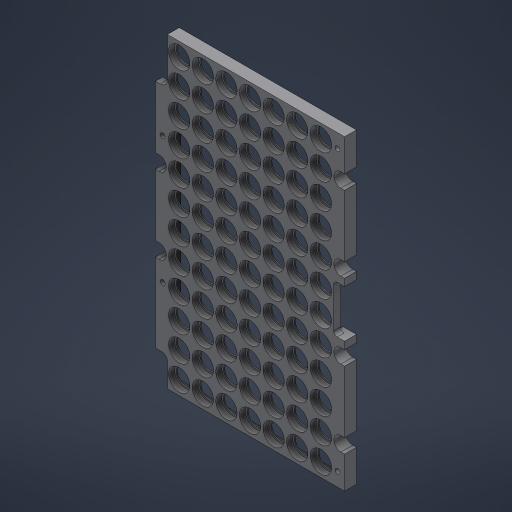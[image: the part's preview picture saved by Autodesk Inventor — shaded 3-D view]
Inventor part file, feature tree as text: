
AUTODESK INVENTOR PART (.ipt)
format: ipt  version: 2024.3 (Build 283343010, 343A)  size: 755,200 bytes
history: native  units: mm
features: extrude x4, sketch x3, hole x3, pattern_linear x1, fillet x1
ambient origin geometry x8: Origin, YZ Plane, XZ Plane, XY Plane, X Axis, Y Axis, Z Axis, Center Point
bodies: Volumenkörper1 (feature_tree)
feature tree (12):
  sketch  "Skizze1"  dims[d0=160.0mm d1=260.0mm]
  extrude  "Extrusion1"  Depth=260.0mm
  hole  "Bohrung1"  [1 undecoded]
  pattern_linear  "Rechteckige Anordnung1"  Count1=6 Spacing1=43.0mm
  sketch  "Skizze2"  dims[d2=10.0mm d3=0.0mm d4=18.0mm d5=60.0mm d7=43.0mm d8=70.0mm d10=20.0mm]
  extrude  "Extrusion4"  Depth=3.0mm
  hole  "Bohrung4"  [1 undecoded]
  sketch  "Skizze4"  dims[d16=21.5mm d19=70.0mm d21=20.0mm d22=60.0mm d24=43.0mm d69=15.0mm d70=15.0mm d71=6.0mm d72=18.0mm d73=5.0mm d74=90.0deg d75=8.0mm d76=20.594885mm d77=70.0mm d79=20.0mm d80=0.0mm d83=10.0mm d84=5.0mm d85=60.0mm d101=25.0mm d113=157.7mm d119=8.0mm d121=6.0mm d124=33.25mm d125=64.5mm d126=6.0mm d127=10.75mm d129=7.0mm d130=7.0mm d132=3.0mm d134=10.75mm d135=9.5mm d136=3.0mm d140=10.0mm d141=0.0mm d142=6.0mm d143=4.0mm d144=5.0mm d145=4.0mm d146=6.0mm d147=4.0mm d148=2.0mm d149=90.0deg d150=8.0mm d151=20.594885mm d152=4.0mm d153=6.0mm d154=6.0mm d155=5.0mm d156=90.0deg d157=8.0mm d158=20.594885mm d160=8.0mm d162=3.0mm d165=20.0mm d166=5.75mm d169=7.0mm d170=7.0mm d171=3.64mm d172=10.75mm d180=2.0mm d181=2.0mm d182=5.0mm d184=8.75mm d185=8.75mm d186=4.0mm d187=0.0mm d190=40.0mm d191=20.0mm d192=0.0mm d193=0.0mm d195=60.0mm d196=60.0mm d197=2.0mm d198=3.0mm d118=0.5mm d120=0.5mm]
  extrude  "Extrusion6"  Depth=3.0mm
  extrude  "Extrusion7"  Depth=3.0mm
  fillet  "Rundung3"  [1 undecoded]
  hole  "Bohrung3"  [1 undecoded]
note: 4 required parameter values undecoded (feature->parameter linkage not recoverable at this tier; creation-order binding heuristic only, values carry confidence <= 0.55)
